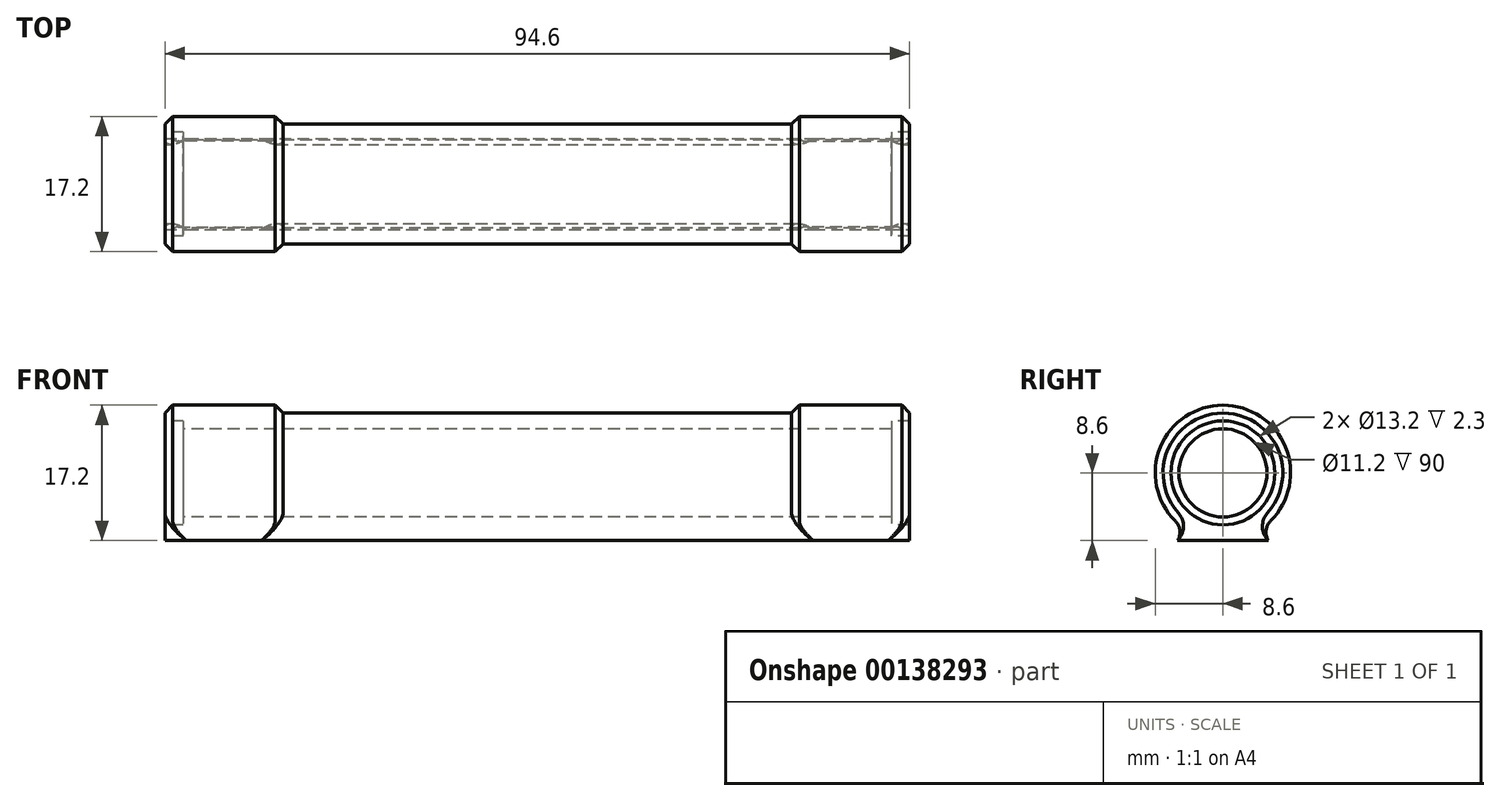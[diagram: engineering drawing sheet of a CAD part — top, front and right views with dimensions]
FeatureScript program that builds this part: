
annotation { "Feature Type Name" : "Feature", "Feature Type Description" : "" }
export const myFeature = defineFeature(function(context is Context, id is Id, definition is map)
    precondition{}
    {
        {
            var Q0;
            Q0=qCreatedBy(makeId("Front.planeOp"),FACE);
            var sketch = newSketch(context, id + "F0", { "sketchPlane" : qUnion([Q0])});
            skLineSegment(sketch, "E0.bottom", {"start": v(-20.03, 0) * mm, "end": v(45, 0) * mm, "construction": true});
            skLineSegment(sketch, "E0.top", {"start": v(0, -7.6) * mm, "end": v(32.3, -7.6) * mm});
            skLineSegment(sketch, "E0.right", {"start": v(47.3, -6.6) * mm, "end": v(47.3, -7.6) * mm});
            skLineSegment(sketch, "E1", {"start": v(47.3, -6.6) * mm, "end": v(45, -6.6) * mm});
            skLineSegment(sketch, "E2", {"start": v(45, -6.6) * mm, "end": v(45, -5.6) * mm});
            skLineSegment(sketch, "E3", {"start": v(45, -5.6) * mm, "end": v(0, -5.6) * mm});
            skLineSegment(sketch, "E4", {"start": v(0, 0) * mm, "end": v(0, -7.6) * mm, "construction": true});
            skLineSegment(sketch, "E5", {"start": v(32.3, -7.6) * mm, "end": v(32.3, -8.6) * mm});
            skLineSegment(sketch, "E6", {"start": v(32.3, -8.6) * mm, "end": v(47.3, -8.6) * mm});
            skLineSegment(sketch, "E7", {"start": v(47.3, -8.6) * mm, "end": v(47.3, -7.6) * mm});
            skLineSegment(sketch, "E8.MirrorCS", {"start": v(-47.3, -6.6) * mm, "end": v(-47.3, -7.6) * mm});
            skLineSegment(sketch, "E9.MirrorCS", {"start": v(-45, -6.6) * mm, "end": v(-45, -5.6) * mm});
            skLineSegment(sketch, "E10.MirrorCS", {"start": v(-47.3, -6.6) * mm, "end": v(-45, -6.6) * mm});
            skLineSegment(sketch, "E11.MirrorCS", {"start": v(-47.3, -8.6) * mm, "end": v(-47.3, -7.6) * mm});
            skLineSegment(sketch, "E12.MirrorCS", {"start": v(-32.3, -8.6) * mm, "end": v(-47.3, -8.6) * mm});
            skLineSegment(sketch, "E13.MirrorCS", {"start": v(-32.3, -7.6) * mm, "end": v(-32.3, -8.6) * mm});
            skLineSegment(sketch, "E14.MirrorCS", {"start": v(-45, -5.6) * mm, "end": v(0, -5.6) * mm});
            skLineSegment(sketch, "E15.MirrorCS", {"start": v(0, -7.6) * mm, "end": v(-32.3, -7.6) * mm});
            skSolve(sketch);
        }
        {
            var Q0;
            Q0=makeQuery(id+"F0.imprint","IMPRINT",FACE,{"disambiguationData":[TD([[makeQuery(id+"F0.imprint","IMPRINT",EDGE,{"derivedFrom":sQuery(id+"F0.wireOp",EDGE,"E0.top")}),1.0]])]});
            var Q1;
            Q1=sQuery(id+"F0.wireOp",EDGE,"E0.bottom");
            revolve(context, id + "F1", {"entities" : qUnion([Q0]), "axis" : qUnion([Q1]), "revolveType" : RevolveType.FULL});
        }
        {
            var Q0;
            Q0=makeQuery(id+"F1.opRevolve","SWEPT_EDGE",EDGE,{"disambiguationData":[OSD([sQuery(id+"F0.wireOp",EDGE,"E5"),sQuery(id+"F0.wireOp",EDGE,"E6")])]});
            var Q1;
            Q1=makeQuery(id+"F1.opRevolve","SWEPT_EDGE",EDGE,{"disambiguationData":[OSD([sQuery(id+"F0.wireOp",EDGE,"E6"),sQuery(id+"F0.wireOp",EDGE,"E7")])]});
            var Q2;
            Q2=makeQuery(id+"F1.opRevolve","SWEPT_EDGE",EDGE,{"disambiguationData":[OSD([sQuery(id+"F0.wireOp",EDGE,"E12.MirrorCS"),sQuery(id+"F0.wireOp",EDGE,"E13.MirrorCS")])]});
            var Q3;
            Q3=makeQuery(id+"F1.opRevolve","SWEPT_EDGE",EDGE,{"disambiguationData":[OSD([sQuery(id+"F0.wireOp",EDGE,"E11.MirrorCS"),sQuery(id+"F0.wireOp",EDGE,"E12.MirrorCS")])]});
            chamfer(context, id + "F2", {"entities" : qUnion([Q0, Q1, Q2, Q3]), "width" : 1 * mm, "tangentPropagation" : true});
        }
        {
            var Q0;
            Q0=makeQuery(id+"F1.opRevolve","SWEPT_FACE",FACE,{"disambiguationData":[OSD([sQuery(id+"F0.wireOp",EDGE,"E0.right"),sQuery(id+"F0.wireOp",EDGE,"E7")])]});
            var sketch = newSketch(context, id + "F3", { "sketchPlane" : qUnion([Q0])});
            skLineSegment(sketch, "E16.bottom", {"start": v(-3.77, -6.6) * mm, "end": v(3.77, -6.6) * mm});
            skLineSegment(sketch, "E17", {"start": v(-3.77, -6.6) * mm, "end": v(-5.77, -8.6) * mm, "construction": true});
            skLineSegment(sketch, "E18", {"start": v(-5.77, -8.6) * mm, "end": v(5.77, -8.6) * mm});
            skLineSegment(sketch, "E19", {"start": v(5.77, -8.6) * mm, "end": v(3.77, -6.6) * mm, "construction": true});
            skArc(sketch, "E20.0", {"start": v(-5.67, -5.06) * mm, "mid": v(-1.22, -7.5) * mm, "end": v(3.77, -6.6) * mm});
            skArc(sketch, "E21", {"start": v(-5.77, -8.6) * mm, "mid": v(-5.01, -6.85) * mm, "end": v(-5.67, -5.06) * mm});
            skArc(sketch, "E22.MirrorCS", {"start": v(5.77, -8.6) * mm, "mid": v(5.01, -6.85) * mm, "end": v(5.67, -5.06) * mm});
            skArc(sketch, "E23.0", {"start": v(3.77, -6.6) * mm, "mid": v(4.78, -5.9) * mm, "end": v(5.67, -5.06) * mm});
            skArc(sketch, "E24.trimOffspring", {"start": v(-5.67, -5.06) * mm, "mid": v(-4.78, -5.9) * mm, "end": v(-3.77, -6.6) * mm});
            skSolve(sketch);
        }
        {
            var Q0;
            Q0 = qSketchRegion(id + "F3", true);
            var Q1;
            Q1 = qConstructionFilter(qBodyType(qCreatedBy(id + "F3" ,EDGE), BodyType.WIRE), ConstructionObject.NO);
            var Q2;
            Q2=makeQuery(id+"F1.opRevolve","SWEPT_FACE",FACE,{"disambiguationData":[OSD([sQuery(id+"F0.wireOp",EDGE,"E8.MirrorCS"),sQuery(id+"F0.wireOp",EDGE,"E11.MirrorCS")])]});
            extrude(context, id + "F4", {"entities" : qUnion([Q0]), "operationType" : NewBodyOperationType.ADD, "surfaceEntities" : qUnion([Q1]), "endBound" : BoundingType.UP_TO_SURFACE, "oppositeDirection" : true, "endBoundEntityFace" : qUnion([Q2]), "depth" : 25 * mm});
        }
        {
            var Q0;
            Q0=makeQuery(id+"F4.boolean.opBoolean","INTERSECT",EDGE,{"derivedFrom":[makeQuery(id+"F1.opRevolve","SWEPT_FACE",FACE,{"disambiguationData":[OSD([sQuery(id+"F0.wireOp",EDGE,"E6")])]}),makeQuery(id+"F4.opExtrude","SWEPT_FACE",FACE,{"disambiguationData":[OSD([sQuery(id+"F3.wireOp",EDGE,"E22.MirrorCS")])]})]});
            var Q1;
            Q1=makeQuery(id+"F4.boolean.opBoolean","INTERSECT",EDGE,{"derivedFrom":[makeQuery(id+"F1.opRevolve","SWEPT_FACE",FACE,{"disambiguationData":[OSD([sQuery(id+"F0.wireOp",EDGE,"E12.MirrorCS")])]}),makeQuery(id+"F4.opExtrude","SWEPT_FACE",FACE,{"disambiguationData":[OSD([sQuery(id+"F3.wireOp",EDGE,"E22.MirrorCS")])]})]});
            var Q2;
            Q2=makeQuery(id+"F4.boolean.opBoolean","INTERSECT",EDGE,{"derivedFrom":[makeQuery(id+"F1.opRevolve","SWEPT_FACE",FACE,{"disambiguationData":[OSD([sQuery(id+"F0.wireOp",EDGE,"E6")])]}),makeQuery(id+"F4.opExtrude","SWEPT_FACE",FACE,{"disambiguationData":[OSD([sQuery(id+"F3.wireOp",EDGE,"E21")])]})]});
            var Q3;
            Q3=makeQuery(id+"F4.boolean.opBoolean","INTERSECT",EDGE,{"derivedFrom":[makeQuery(id+"F1.opRevolve","SWEPT_FACE",FACE,{"disambiguationData":[OSD([sQuery(id+"F0.wireOp",EDGE,"E12.MirrorCS")])]}),makeQuery(id+"F4.opExtrude","SWEPT_FACE",FACE,{"disambiguationData":[OSD([sQuery(id+"F3.wireOp",EDGE,"E21")])]})]});
            fillet(context, id + "F5", {"entities" : qUnion([Q0, Q1, Q2, Q3]), "radius" : 2 * mm, "tangentPropagation" : true, "allowEdgeOverflow" : false});
        }
    });
